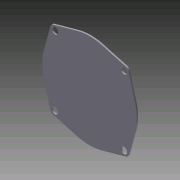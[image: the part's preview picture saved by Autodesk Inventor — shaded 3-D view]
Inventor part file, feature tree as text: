
AUTODESK INVENTOR PART (.ipt)
format: ipt  version: 2011 (Build 150239000, 239)  size: 87,552 bytes
history: native  units: in
note: dims shown in document units (in); Inventor stores cm internally (conversion verified against a paired STEP export)
features: extrude x1, sketch x1
ambient origin geometry x8: Origin, YZ Plane, XZ Plane, XY Plane, X Axis, Y Axis, Z Axis, Center Point
bodies: Solid1 (feature_tree)
feature tree (2):
  extrude  "Extrusion1"  [1 undecoded]
  sketch  "Sketch1"  dims[d0=0.05in d1=0.0in]
note: 1 required parameter value undecoded (feature->parameter linkage not recoverable at this tier; creation-order binding heuristic only, values carry confidence <= 0.55)
